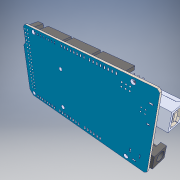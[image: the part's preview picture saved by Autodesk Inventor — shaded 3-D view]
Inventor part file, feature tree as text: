
AUTODESK INVENTOR PART (.ipt)
format: ipt  version: 2019 (Build 230136000, 136)  size: 1,265,664 bytes
history: mixed  units: mm
features: other x1, fillet x1, imported_body x1
ambient origin geometry x8: Origin, YZ Plane, XZ Plane, XY Plane, X Axis, Y Axis, Z Axis, Center Point
bodies: Body1 (imported_parasolid)
feature tree (3):
  other  "Твердое тело1"
  fillet  "Fillet5"  [1 undecoded]
  imported_body  NMx_Import_Brep_tag  [imported B-rep: ~376 faces, bbox_mm=[107.95, 53.4162, 12.928185]]
note: 1 required parameter value undecoded (feature->parameter linkage not recoverable at this tier; creation-order binding heuristic only, values carry confidence <= 0.55)
